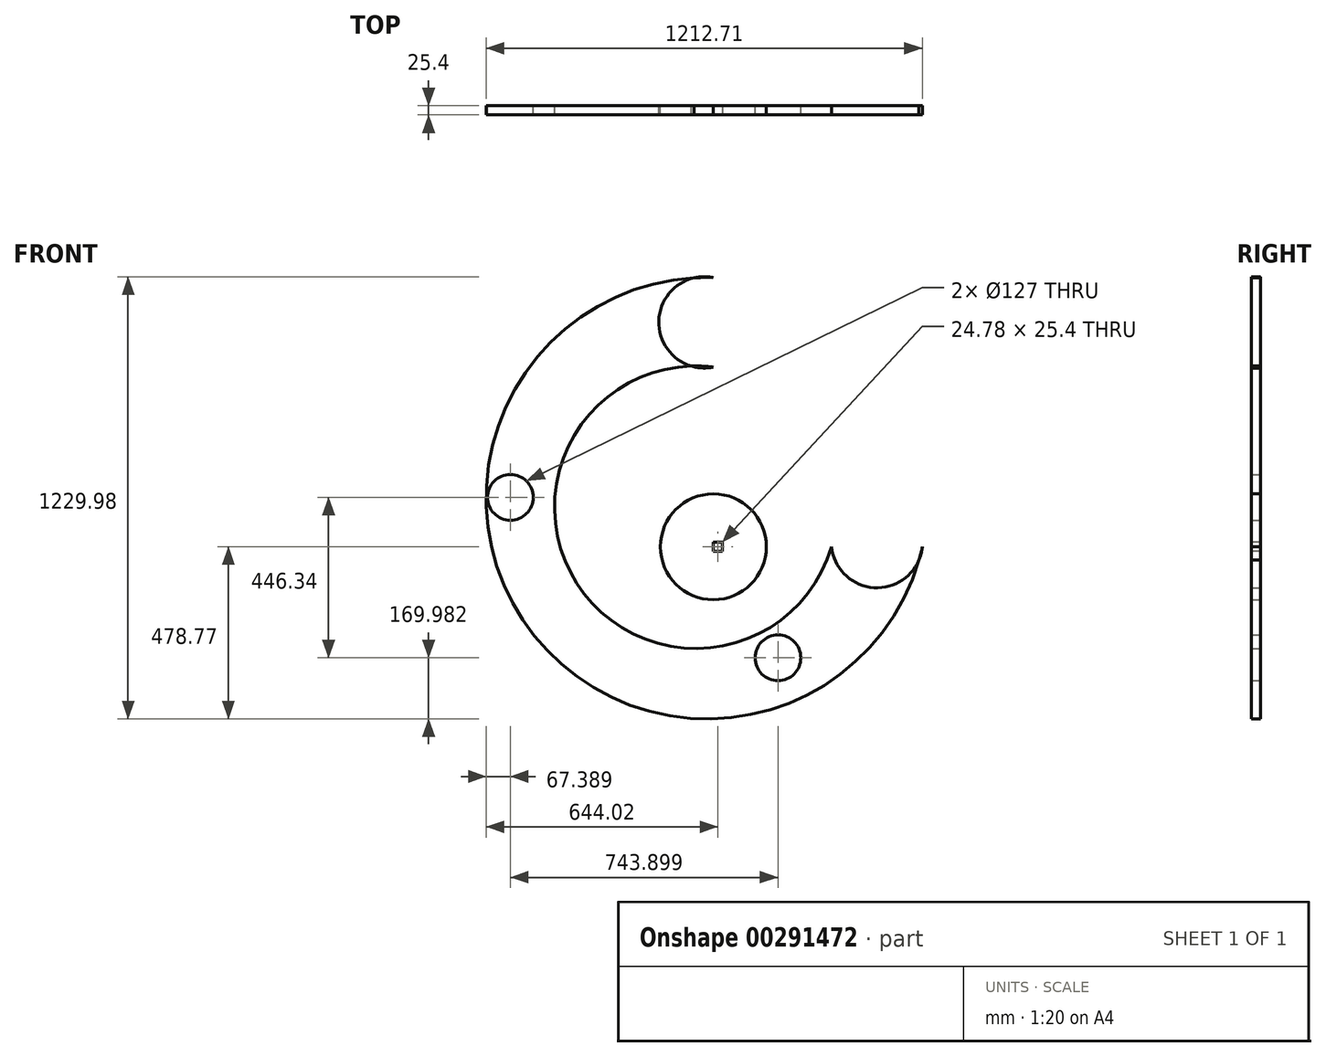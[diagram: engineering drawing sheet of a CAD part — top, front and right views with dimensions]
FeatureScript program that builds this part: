
annotation { "Feature Type Name" : "Feature", "Feature Type Description" : "" }
export const myFeature = defineFeature(function(context is Context, id is Id, definition is map)
    precondition{}
    {
        {
            var Q0;
            Q0=qCreatedBy(makeId("Front.planeOp"),FACE);
            var sketch = newSketch(context, id + "F0", { "sketchPlane" : qUnion([Q0])});
            skArc(sketch, "E0", {"start": v(0, 748.74) * mm, "mid": v(-502.72, -241.26) * mm, "end": v(581.08, 0) * mm});
            skArc(sketch, "E1", {"start": v(0, 499.68) * mm, "mid": v(-376.92, -105.85) * mm, "end": v(328.44, 0) * mm});
            skCircle(sketch, "E2", {"center": v(0, 0) * mm, "radius": 147.18 * mm});
            skCircle(sketch, "E3", {"center": v(-564.24, 137.55) * mm, "radius": 63.5 * mm});
            skCircle(sketch, "E4", {"center": v(179.66, -308.79) * mm, "radius": 63.5 * mm});
            skArc(sketch, "E5", {"start": v(328.44, 0) * mm, "mid": v(454.76, -113.9) * mm, "end": v(581.08, 0) * mm});
            skArc(sketch, "E6", {"start": v(0, 748.74) * mm, "mid": v(-151.9, 624.2) * mm, "end": v(0, 499.68) * mm});
            skSolve(sketch);
        }
        {
            var Q0;
            Q0 = qSketchRegion(id + "F0", true);
            extrude(context, id + "F1", {"entities" : qUnion([Q0]), "depth" : 25.4 * mm});
        }
        {
            var Q0;
            Q0=qCreatedBy(makeId("Top.planeOp"),FACE);
            var sketch = newSketch(context, id + "F2", { "sketchPlane" : qUnion([Q0])});
            skLineSegment(sketch, "E7", {"start": v(24.78, 0) * mm, "end": v(24.78, -25.41) * mm});
            skLineSegment(sketch, "E8", {"start": v(24.78, -25.41) * mm, "end": v(13.86, -25.41) * mm});
            skLineSegment(sketch, "E9", {"start": v(13.86, -25.41) * mm, "end": v(13.86, -42.42) * mm});
            skLineSegment(sketch, "E10", {"start": v(13.86, -42.42) * mm, "end": v(0, -42.42) * mm});
            skLineSegment(sketch, "E11", {"start": v(0, -42.42) * mm, "end": v(0, 0) * mm});
            skLineSegment(sketch, "E12", {"start": v(0, 0) * mm, "end": v(24.78, 0) * mm});
            skSolve(sketch);
        }
        {
            var Q0;
            Q0 = qSketchRegion(id + "F2", true);
            extrude(context, id + "F3", {"entities" : qUnion([Q0]), "operationType" : NewBodyOperationType.REMOVE, "endBound" : BoundingType.SYMMETRIC, "oppositeDirection" : true, "depth" : 25.4 * mm});
        }
    });
